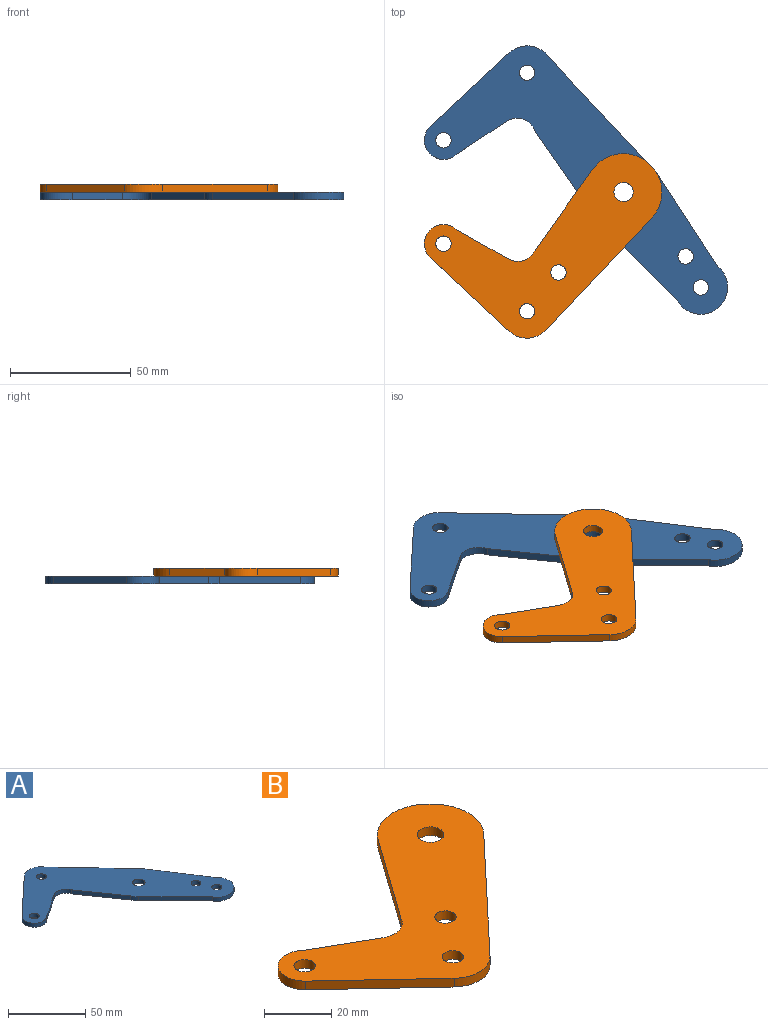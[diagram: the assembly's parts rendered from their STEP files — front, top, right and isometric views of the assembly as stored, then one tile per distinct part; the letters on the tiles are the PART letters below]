
ASSEMBLY  parts=2 mates=1
PART A: 18 faces, bbox 125.5x111.1x3.2 mm
  f0: plane 31.92x22.29mm, normal (-0.82,-0.57,0), area 123.6mm2, adj f1,f14,f16,f17
  f1: cylinder r=15.88mm len=4.39mm, axis (0,0,-1), area 17.1mm2, adj f0,f2,f16,f17
  f2: plane 33.88x33.63mm, normal (-0.71,-0.7,0), area 151.6mm2, adj f1,f3,f16,f17
  f3: cylinder r=11.11mm len=20.72mm, axis (0,0,-1), area 123.8mm2, adj f2,f4,f16,f17
  f4: plane 39.47x25.62mm, normal (0.84,0.54,0), area 149.4mm2, adj f3,f5,f16,f17
  f5: plane 46.81x43.99mm, normal (0.73,0.68,0), area 203.9mm2, adj f4,f6,f16,f17
  f6: cylinder r=11.11mm len=16.88mm, axis (0,0,-1), area 61.4mm2, adj f5,f7,f16,f17
  f7: plane 32.38x30.29mm, normal (-0.68,0.73,0), area 140.8mm2, adj f6,f8,f16,f17
  f8: cylinder r=7.94mm len=13.73mm, axis (0,0,-1), area 79.1mm2, adj f7,f9,f16,f17
  f9: plane 20.54x13.63mm, normal (0.55,-0.83,0), area 78.3mm2, adj f8,f14,f16,f17
  f10: cylinder r=3.17mm len=6.35mm, axis (0,0,-1), area 63.3mm2, adj f16,f17
  f11: cylinder r=3.98mm len=7.95mm, axis (0,0,-1), area 79.3mm2, adj f16,f17
  f12: cylinder r=3.17mm len=6.35mm, axis (0,0,-1), area 63.3mm2, adj f16,f17
  f13: cylinder r=3.17mm len=6.35mm, axis (0,0,-1), area 63.3mm2, adj f16,f17
  f14: cylinder r=7.95mm len=11.92mm, axis (0,0,-1), area 46.2mm2, adj f0,f9,f16,f17
  f15: cylinder r=3.17mm len=6.35mm, axis (0,0,-1), area 63.3mm2, adj f16,f17
  f16: plane 125.52x111.06mm, normal (0,0,1), area 4013.2mm2, adj f0,f1,f2,f3,f4,f5,f6,f7
  f17: plane 125.52x111.06mm, normal (0,0,-1), area 4013.2mm2, adj f0,f1,f2,f3,f4,f5,f6,f7
PART B: 16 faces, bbox 98.3x76.3x3.2 mm
  f0: cylinder r=15.88mm len=22.39mm, axis (0,0,1), area 80.2mm2, adj f1,f11,f14,f15
  f1: plane 33.32x23.69mm, normal (-0.82,0.58,0), area 129.8mm2, adj f0,f2,f14,f15
  f2: cylinder r=7.95mm len=11.13mm, axis (0,0,1), area 41.7mm2, adj f1,f3,f14,f15
  f3: plane 21.31x12.08mm, normal (0.49,0.87,0), area 77.8mm2, adj f2,f4,f14,f15
  f4: cylinder r=7.94mm len=13.73mm, axis (0,0,1), area 79.3mm2, adj f3,f5,f14,f15
  f5: plane 32.38x30.29mm, normal (-0.68,-0.73,0), area 140.8mm2, adj f4,f6,f14,f15
  f6: cylinder r=11.11mm len=15.68mm, axis (0,0,1), area 55.3mm2, adj f5,f7,f14,f15
  f7: plane 46.08x43.43mm, normal (0.73,-0.69,0), area 201mm2, adj f6,f8,f14,f15
  f8: cylinder r=15.88mm len=19.53mm, axis (0,0,1), area 67.1mm2, adj f7,f11,f14,f15
  f9: cylinder r=3.17mm len=6.35mm, axis (0,0,1), area 63.3mm2, adj f14,f15
  f10: cylinder r=3.17mm len=6.35mm, axis (0,0,1), area 63.3mm2, adj f14,f15
  f11: plane 4.11x3.86mm, normal (0.73,0.68,0), area 17.9mm2, adj f0,f8,f14,f15
  f12: cylinder r=3.98mm len=7.95mm, axis (0,0,1), area 79.3mm2, adj f14,f15
  f13: cylinder r=3.17mm len=6.35mm, axis (0,0,1), area 63.3mm2, adj f14,f15
  f14: plane 98.32x76.34mm, normal (0,0,-1), area 2960mm2, adj f0,f1,f2,f3,f4,f5,f6,f7
  f15: plane 98.32x76.34mm, normal (0,0,1), area 2960mm2, adj f0,f1,f2,f3,f4,f5,f6,f7
PLACE A at identity fixed
PLACE B t=(0,0,6.35)mm
MATE revolute B.f12 <-> A.f11  axis (0,0,-1) through (0,0,3.18)mm
